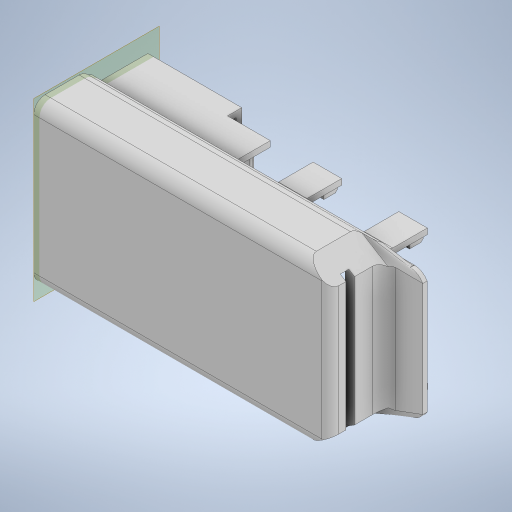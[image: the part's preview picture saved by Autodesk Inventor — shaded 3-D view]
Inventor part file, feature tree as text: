
AUTODESK INVENTOR PART (.ipt)
format: ipt  version: 2023.3 (Build 273359000, 359)  size: 830,976 bytes
history: native  units: mm
features: reference x27, extrude x16, sketch x16, fillet x9, thicken_offset x4, other x4, plane x2, loft x1, chamfer x1, projected_geometry x1
ambient origin geometry x8: Origin, YZ Plane, XZ Plane, XY Plane, X Axis, Y Axis, Z Axis, Center Point
bodies: Solid1 (feature_tree)
feature tree (81):
  extrude  "fastening_tabs"  TaperAngle=0.0deg  [1 undecoded]
  extrude  "Extrusion2"  TaperAngle=0.0deg  [1 undecoded]
  plane  "Work Plane2"
  sketch  "Sketch3"  dims[d2=0.0mm d3=0.0mm]
  extrude  "Extrusion3"  TaperAngle=0.0deg  [1 undecoded]
  loft  "Loft2"
  extrude  "Extrusion4"  Depth=0.3mm TaperAngle=0.0deg
  extrude  "Extrusion5"  Depth=0.4mm
  extrude  "Extrusion6"  Depth=0.4mm TaperAngle=0.0deg
  extrude  "Extrusion7"  Depth=2.8mm TaperAngle=0.0deg
  extrude  "Extrusion8"  Depth=0.4mm TaperAngle=0.0deg
  sketch  "Sketch12"  dims[d37=3.3mm d38=0.0mm d39=0.4mm d40=0.0mm]
  sketch  "Sketch13"  dims[d45=19.0mm d46=1.777mm]
  extrude  "Extrusion9"  Depth=1.777mm
  extrude  "Extrusion10"  Depth=0.2mm
  chamfer  "Chamfer1"  Distance=2.8mm
  fillet  "Fillet4"  Radius=1.0mm
  extrude  "Extrusion13"  Depth=0.35mm TaperAngle=0.0deg
  extrude  "Extrusion14"  Depth=0.9mm
  extrude  "Extrusion15"  Depth=0.4mm TaperAngle=0.0deg
  extrude  "Extrusion16"  Depth=0.2mm
  fillet  "Fillet5"  Radius=2.0mm
  thicken_offset  "Thicken3"
  thicken_offset  "Thicken4"
  fillet  "Fillet13"  Radius=15.5mm
  fillet  "Fillet14"  Radius=0.8mm
  plane  "Work Plane4"
  extrude  "Extrusion17"  TaperAngle=0.0deg  [1 undecoded]
  fillet  "Fillet16"  [1 undecoded]
  extrude  "Extrusion18"  Depth=0.3mm
  fillet  "Fillet17"  Radius=9.5mm
  fillet  "Fillet18"  Radius=0.6mm
  fillet  "Fillet19"  Radius=1.1mm
  thicken_offset  "Thicken5"
  thicken_offset  "Thicken6"
  fillet  "Fillet20"  Radius=3.0mm
  sketch  "Sketch2"  dims[d0=0.0mm d1=0.0mm]
  sketch  "Sketch5"  dims[d4=0.0mm d5=0.0mm]
  reference  "Reference17"
  reference  "Reference18"
  reference  "Reference19"
  reference  "Reference20"
  sketch  "Sketch6"  dims[d7=0.0mm d8=0.4mm]
  sketch  "Sketch8"  dims[d9=2.3mm d10=0.0mm d12=0.3mm d13=0.0mm]
  sketch  "Sketch9"  dims[d15=0.5mm d16=0.4mm]
  sketch  "Sketch10"  dims[d17=0.4mm d28=2.8mm d29=0.0mm]
  reference  "Reference22"
  sketch  "Sketch11"  dims[d33=0.0mm d34=90.0deg d35=2.8mm d36=0.0mm]
  reference  "Reference23"
  reference  "Reference24"
  reference  "Reference25"
  reference  "Reference26"
  sketch  "Sketch17"  dims[d48=0.2mm d49=0.2mm d50=2.8mm d51=0.0mm d52=1.0mm d53=0.0mm]
  sketch  "Sketch18"  dims[d62=0.35mm d63=0.0mm d64=0.35mm d65=0.0mm]
  projected_geometry  "Projected Loop1"
  sketch  "Sketch19"  dims[d66=0.15mm d67=2.0mm d68=45.0deg d69=0.9mm]
  reference  "Reference27"
  reference  "Reference28"
  reference  "Reference29"
  reference  "Reference30"
  reference  "Reference31"
  reference  "Reference32"
  reference  "Reference33"
  reference  "Reference34"
  reference  "Reference35"
  reference  "Reference36"
  reference  "Reference37"
  sketch  "Sketch20"  dims[d83=0.4mm d85=0.5mm d86=0.0mm]
  reference  "Reference38"
  reference  "Reference39"
  reference  "Reference41"
  reference  "Reference42"
  reference  "Reference44"
  reference  "Reference45"
  other  "Edges3"
  reference  "Reference46"
  sketch  "Sketch21"  dims[d87=0.5mm d88=0.0mm d89=0.2mm d90=2.0mm d91=0.0mm d92=15.5mm d93=0.8mm]
  sketch  "Sketch22"  dims[d94=0.8mm d95=0.0mm d96=0.0mm d100=10.4mm d101=9.5mm d102=0.6mm d103=1.1mm d104=3.0mm d105=0.0mm d115=0.25mm d116=0.25mm d117=0.1mm d118=0.1mm d120=0.1mm d122=0.1mm d126=1.0mm d127=1.0mm d128=0.25mm d129=0.0mm d130=90.0deg d131=0.8mm d134=0.15mm d135=0.15mm d136=0.15mm d137=0.15mm d141=0.7mm d142=0.5mm d143=-0.4mm d146=0.3mm d147=1.0mm d148=1.0mm d149=1.8mm d150=0.3mm d151=0.0mm d152=0.6mm d153=6.0mm d154=1.2mm d155=5.0mm d156=0.3mm d157=0.0mm d158=0.1mm d159=0.3mm d160=0.0mm d161=0.3mm d162=0.3mm d163=0.3mm d164=0.3mm d165=0.3mm d166=0.3mm d167=0.3mm d18=0.872665mm d30=0.5mm d31=0.872665mm d43=0.0mm d44=0.0mm d107=0.0mm d108=0.0mm d109=0.0mm d110=0.0mm d123=0.5mm d124=0.872665mm d125=0.5mm]
  parser-record x1  (decoder bookkeeping rows leaked as tree rows — omitted from the tree; the rows remain in map.json)
  other  "np2a_assembly.iam"
  other  "np2a:1"
note: 5 required parameter values undecoded (feature->parameter linkage not recoverable at this tier; creation-order binding heuristic only, values carry confidence <= 0.55)
note: 1 file-system path scrubbed to <path> (originals preserved in map.json)
